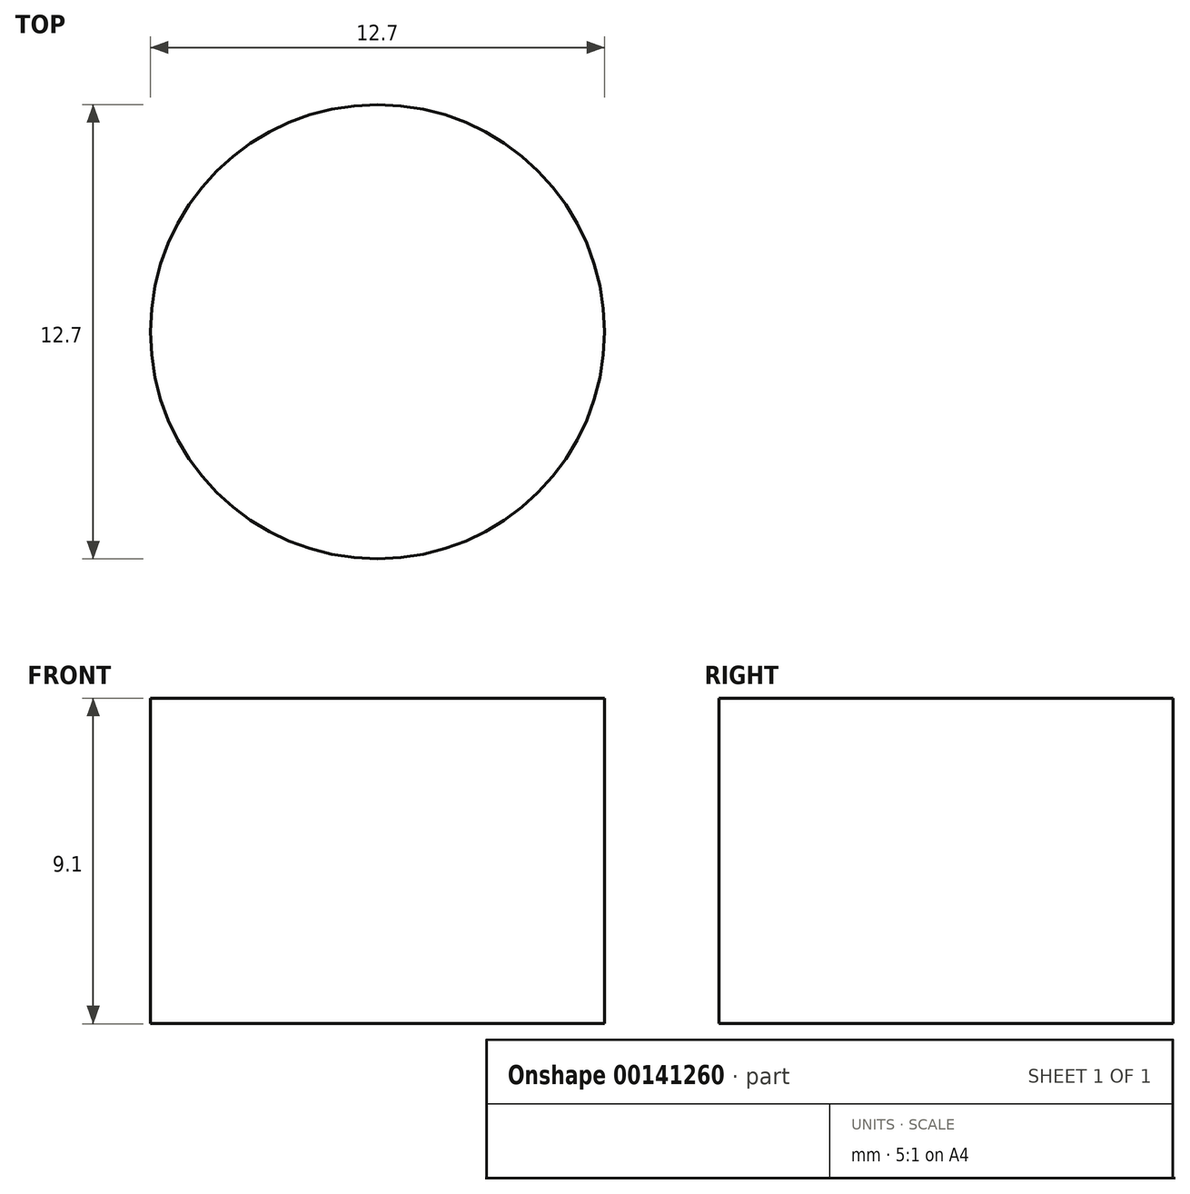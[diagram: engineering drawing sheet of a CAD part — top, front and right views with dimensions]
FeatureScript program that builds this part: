
annotation { "Feature Type Name" : "Feature", "Feature Type Description" : "" }
export const myFeature = defineFeature(function(context is Context, id is Id, definition is map)
    precondition{}
    {
        {
            var Q0;
            Q0=qCreatedBy(makeId("Front.planeOp"),FACE);
            var sketch = newSketch(context, id + "F0", { "sketchPlane" : qUnion([Q0])});
            skLineSegment(sketch, "E0.bottom", {"start": v(-41.88, 37.24) * mm, "end": v(-35.53, 37.24) * mm});
            skLineSegment(sketch, "E0.top", {"start": v(-41.88, 28.14) * mm, "end": v(-35.53, 28.14) * mm});
            skLineSegment(sketch, "E0.left", {"start": v(-41.88, 37.24) * mm, "end": v(-41.88, 28.14) * mm});
            skLineSegment(sketch, "E0.right", {"start": v(-35.53, 37.24) * mm, "end": v(-35.53, 28.14) * mm});
            skSolve(sketch);
        }
        {
            var Q0;
            Q0=makeQuery(id+"F0.imprint","IMPRINT",FACE,{"disambiguationData":[TD([[makeQuery(id+"F0.imprint","IMPRINT",EDGE,{"derivedFrom":sQuery(id+"F0.wireOp",EDGE,"E0.bottom")}),-1.0]])]});
            var Q1;
            Q1=sQuery(id+"F0.wireOp",EDGE,"E0.left");
            revolve(context, id + "F1", {"entities" : qUnion([Q0]), "axis" : qUnion([Q1]), "revolveType" : RevolveType.FULL});
        }
    });
